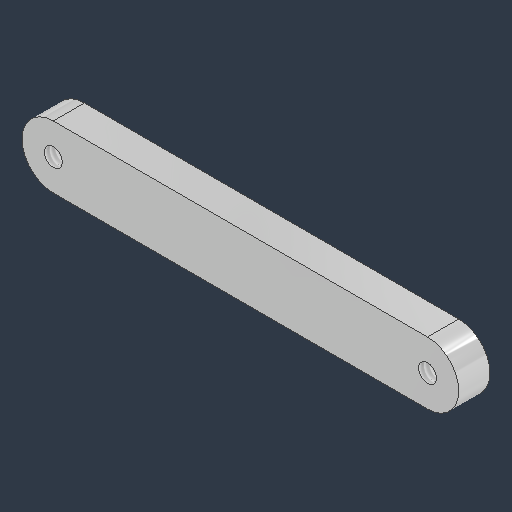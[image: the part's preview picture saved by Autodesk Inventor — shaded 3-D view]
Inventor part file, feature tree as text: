
AUTODESK INVENTOR PART (.ipt)
format: ipt  version: 2024.3 (Build 283343000, 343)  size: 124,928 bytes
history: native  units: in
note: dims shown in document units (in); Inventor stores cm internally (conversion verified against a paired STEP export)
features: sketch x2, sheet_metal_op x1, chamfer x1, hole x1, other x1
ambient origin geometry x8: Origin, YZ Plane, XZ Plane, XY Plane, X Axis, Y Axis, Z Axis, Center Point
bodies: Solid1 (feature_tree)
feature tree (6):
  sheet_metal_op  "Face1"
  chamfer  "Corner Round1"
  hole  "Hole1"  [1 undecoded]
  sketch  "Sketch1"  dims[d0=3.5in d1=0.5in]
  other  "Plate1"
  sketch  "Sketch4"  dims[d2=0.25in d23=0.25in d24=0.145in d25=0.38in d26=0.375in d27=0.19in d28=0.5635in d29=0.25in d30=0.8108in]
note: 1 required parameter value undecoded (feature->parameter linkage not recoverable at this tier; creation-order binding heuristic only, values carry confidence <= 0.55)
